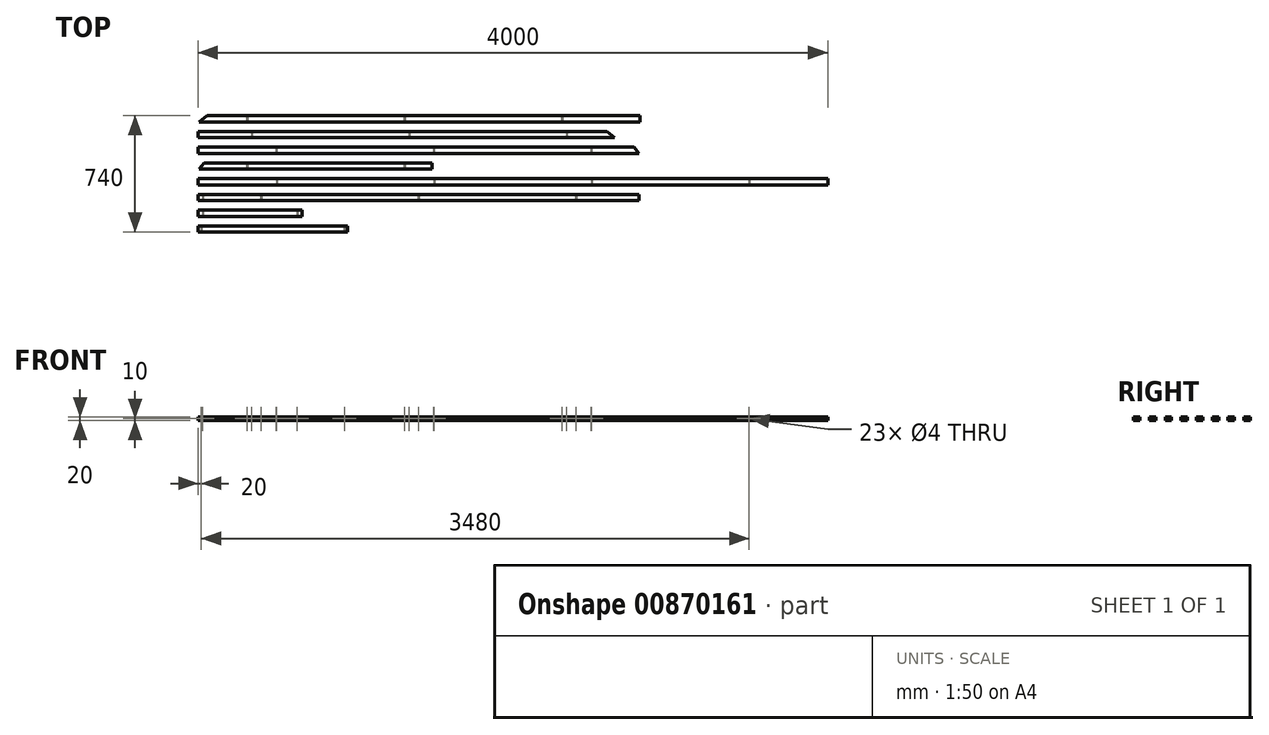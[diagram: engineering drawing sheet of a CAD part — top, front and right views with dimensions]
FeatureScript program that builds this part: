
annotation { "Feature Type Name" : "Feature", "Feature Type Description" : "" }
export const myFeature = defineFeature(function(context is Context, id is Id, definition is map)
    precondition{}
    {
        {
            var Q0;
            Q0=qCreatedBy(makeId("Right.planeOp"),FACE);
            var sketch = newSketch(context, id + "F0", { "sketchPlane" : qUnion([Q0])});
            skLineSegment(sketch, "E0.bottom", {"start": v(0, 0) * mm, "end": v(-40, 0) * mm});
            skLineSegment(sketch, "E0.top", {"start": v(0, 20) * mm, "end": v(-40, 20) * mm});
            skLineSegment(sketch, "E0.left", {"start": v(0, 0) * mm, "end": v(0, 20) * mm});
            skLineSegment(sketch, "E0.right", {"start": v(-40, 0) * mm, "end": v(-40, 20) * mm});
            skLineSegment(sketch, "E1.1.0.0", {"start": v(-100, 0) * mm, "end": v(-100, 20) * mm});
            skLineSegment(sketch, "E1.1.0.1", {"start": v(-100, 20) * mm, "end": v(-140, 20) * mm});
            skLineSegment(sketch, "E1.1.0.2", {"start": v(-140, 0) * mm, "end": v(-140, 20) * mm});
            skLineSegment(sketch, "E1.1.0.3", {"start": v(-100, 0) * mm, "end": v(-140, 0) * mm});
            skLineSegment(sketch, "E1.2.0.0", {"start": v(-200, 0) * mm, "end": v(-200, 20) * mm});
            skLineSegment(sketch, "E1.2.0.1", {"start": v(-200, 20) * mm, "end": v(-240, 20) * mm});
            skLineSegment(sketch, "E1.2.0.2", {"start": v(-240, 0) * mm, "end": v(-240, 20) * mm});
            skLineSegment(sketch, "E1.2.0.3", {"start": v(-200, 0) * mm, "end": v(-240, 0) * mm});
            skLineSegment(sketch, "E1.3.0.0", {"start": v(-300, 0) * mm, "end": v(-300, 20) * mm});
            skLineSegment(sketch, "E1.3.0.1", {"start": v(-300, 20) * mm, "end": v(-340, 20) * mm});
            skLineSegment(sketch, "E1.3.0.2", {"start": v(-340, 0) * mm, "end": v(-340, 20) * mm});
            skLineSegment(sketch, "E1.3.0.3", {"start": v(-300, 0) * mm, "end": v(-340, 0) * mm});
            skLineSegment(sketch, "E1.4.0.0", {"start": v(-400, 0) * mm, "end": v(-400, 20) * mm});
            skLineSegment(sketch, "E1.4.0.1", {"start": v(-400, 20) * mm, "end": v(-440, 20) * mm});
            skLineSegment(sketch, "E1.4.0.2", {"start": v(-440, 0) * mm, "end": v(-440, 20) * mm});
            skLineSegment(sketch, "E1.4.0.3", {"start": v(-400, 0) * mm, "end": v(-440, 0) * mm});
            skLineSegment(sketch, "E1.5.0.0", {"start": v(-500, 0) * mm, "end": v(-500, 20) * mm});
            skLineSegment(sketch, "E1.5.0.1", {"start": v(-500, 20) * mm, "end": v(-540, 20) * mm});
            skLineSegment(sketch, "E1.5.0.2", {"start": v(-540, 0) * mm, "end": v(-540, 20) * mm});
            skLineSegment(sketch, "E1.5.0.3", {"start": v(-500, 0) * mm, "end": v(-540, 0) * mm});
            skLineSegment(sketch, "E1.6.0.0", {"start": v(-600, 0) * mm, "end": v(-600, 20) * mm});
            skLineSegment(sketch, "E1.6.0.1", {"start": v(-600, 20) * mm, "end": v(-640, 20) * mm});
            skLineSegment(sketch, "E1.6.0.2", {"start": v(-640, 0) * mm, "end": v(-640, 20) * mm});
            skLineSegment(sketch, "E1.6.0.3", {"start": v(-600, 0) * mm, "end": v(-640, 0) * mm});
            skLineSegment(sketch, "E1.7.0.0", {"start": v(-700, 0) * mm, "end": v(-700, 20) * mm});
            skLineSegment(sketch, "E1.7.0.1", {"start": v(-700, 20) * mm, "end": v(-740, 20) * mm});
            skLineSegment(sketch, "E1.7.0.2", {"start": v(-740, 0) * mm, "end": v(-740, 20) * mm});
            skLineSegment(sketch, "E1.7.0.3", {"start": v(-700, 0) * mm, "end": v(-740, 0) * mm});
            skLineSegment(sketch, "E1.8.0.0", {"start": v(-800, 0) * mm, "end": v(-800, 20) * mm});
            skLineSegment(sketch, "E1.8.0.1", {"start": v(-800, 20) * mm, "end": v(-840, 20) * mm});
            skLineSegment(sketch, "E1.8.0.2", {"start": v(-840, 0) * mm, "end": v(-840, 20) * mm});
            skLineSegment(sketch, "E1.8.0.3", {"start": v(-800, 0) * mm, "end": v(-840, 0) * mm});
            skLineSegment(sketch, "E1.9.0.0", {"start": v(-900, 0) * mm, "end": v(-900, 20) * mm});
            skLineSegment(sketch, "E1.9.0.1", {"start": v(-900, 20) * mm, "end": v(-940, 20) * mm});
            skLineSegment(sketch, "E1.9.0.2", {"start": v(-940, 0) * mm, "end": v(-940, 20) * mm});
            skLineSegment(sketch, "E1.9.0.3", {"start": v(-900, 0) * mm, "end": v(-940, 0) * mm});
            skLineSegment(sketch, "E1.direction1", {"start": v(0, 0) * mm, "end": v(-100, 0) * mm, "construction": true});
            skSolve(sketch);
        }
        {
            var Q0;
            Q0=makeQuery(id+"F0.imprint","IMPRINT",FACE,{"disambiguationData":[TD([[makeQuery(id+"F0.imprint","IMPRINT",EDGE,{"derivedFrom":sQuery(id+"F0.wireOp",EDGE,"E0.bottom")}),-1.0]])]});
            extrude(context, id + "F1", {"entities" : qUnion([Q0]), "depth" : 2807 * mm, "offsetDistance" : 25 * mm});
        }
        {
            var Q0;
            Q0=makeQuery(id+"F1.opExtrude","SWEPT_FACE",FACE,{"disambiguationData":[OSD([sQuery(id+"F0.wireOp",EDGE,"E0.top")])]});
            var sketch = newSketch(context, id + "F2", { "sketchPlane" : qUnion([Q0])});
            skLineSegment(sketch, "E2", {"start": v(0, 0) * mm, "end": v(0, -40) * mm});
            skLineSegment(sketch, "E3", {"start": v(0, -40) * mm, "end": v(49.4, 0) * mm, "construction": true});
            skLineSegment(sketch, "E4", {"start": v(49.4, 0) * mm, "end": v(0, 0) * mm});
            skLineSegment(sketch, "E5", {"start": v(0, -40) * mm, "end": v(10.27, 8.32) * mm, "construction": true});
            skLineSegment(sketch, "E6", {"start": v(0, -40) * mm, "end": v(49.4, -40) * mm, "construction": true});
            skLineSegment(sketch, "E7", {"start": v(49.4, -40) * mm, "end": v(49.4, 0) * mm, "construction": true});
            skLineSegment(sketch, "E8", {"start": v(49.4, 0) * mm, "end": v(10.27, 8.32) * mm, "construction": true});
            skLineSegment(sketch, "E9", {"start": v(6.36, -40) * mm, "end": v(55.75, 0) * mm});
            skLineSegment(sketch, "E10", {"start": v(55.75, 0) * mm, "end": v(49.4, 0) * mm});
            skLineSegment(sketch, "E11", {"start": v(6.36, -40) * mm, "end": v(0, -40) * mm});
            skSolve(sketch);
        }
        {
            var Q0;
            Q0 = qSketchRegion(id + "F2", true);
            extrude(context, id + "F3", {"entities" : qUnion([Q0]), "operationType" : NewBodyOperationType.REMOVE, "endBound" : BoundingType.THROUGH_ALL, "oppositeDirection" : true, "depth" : 25 * mm, "offsetDistance" : 25 * mm});
        }
        {
            var Q0;
            Q0=makeQuery(id+"F1.opExtrude","SWEPT_FACE",FACE,{"disambiguationData":[OSD([sQuery(id+"F0.wireOp",EDGE,"E0.right")])]});
            var sketch = newSketch(context, id + "F4", { "sketchPlane" : qUnion([Q0])});
            skLineSegment(sketch, "E12.bottom", {"start": v(2281, 850) * mm, "end": v(2341, 850) * mm, "construction": true});
            skLineSegment(sketch, "E12.top", {"start": v(2281, -150) * mm, "end": v(2341, -150) * mm, "construction": true});
            skLineSegment(sketch, "E12.left", {"start": v(2281, 850) * mm, "end": v(2281, -150) * mm, "construction": true});
            skLineSegment(sketch, "E12.right", {"start": v(2341, 850) * mm, "end": v(2341, -150) * mm, "construction": true});
            skLineSegment(sketch, "E13", {"start": v(2311, -150) * mm, "end": v(2311, 0) * mm, "construction": true});
            skLineSegment(sketch, "E14", {"start": v(2311, 0) * mm, "end": v(2311, 10) * mm, "construction": true});
            skLineSegment(sketch, "E15", {"start": v(2311, 10) * mm, "end": v(2311, 20) * mm, "construction": true});
            skLineSegment(sketch, "E16.1.0.0", {"start": v(1311, 0) * mm, "end": v(1311, 10) * mm, "construction": true});
            skLineSegment(sketch, "E16.2.0.0", {"start": v(311, 0) * mm, "end": v(311, 10) * mm, "construction": true});
            skLineSegment(sketch, "E16.direction1", {"start": v(2311, 0) * mm, "end": v(1311, 0) * mm, "construction": true});
            skSolve(sketch);
        }
        {
            var Q0;
            Q0=sQuery(id+"F4.wireOp",VERTEX,"E14.end");
            var Q1;
            Q1=sQuery(id+"F4.wireOp",VERTEX,"E16.1.0.0.end");
            var Q2;
            Q2=sQuery(id+"F4.wireOp",VERTEX,"E16.2.0.0.end");
            var Q3;
            Q3=makeQuery(id+"F1.opExtrude","SWEPT_BODY",BODY,{"disambiguationData":[OSD([sQuery(id+"F0.wireOp",EDGE,"E0.bottom"),sQuery(id+"F0.wireOp",EDGE,"E0.top"),sQuery(id+"F0.wireOp",EDGE,"E0.left"),sQuery(id+"F0.wireOp",EDGE,"E0.right")])]});
            hole(context, id + "F5", {"style" : HoleStyle.C_SINK, "endStyle" : HoleEndStyle.THROUGH, "holeDiameter" : 4 * mm, "cSinkDiameter" : 8 * mm, "cSinkAngle" : 90 * degree, "majorDiameter" : 5 * mm, "isTappedThrough" : true, "tappedDepth" : 12 * mm, "tapClearance" : 3, "locations" : qUnion([Q0, Q1, Q2]), "scope" : qUnion([Q3])});
        }
        {
            var Q0;
            Q0=makeQuery(id+"F0.imprint","IMPRINT",FACE,{"disambiguationData":[TD([[makeQuery(id+"F0.imprint","IMPRINT",EDGE,{"derivedFrom":sQuery(id+"F0.wireOp",EDGE,"E1.1.0.0")}),1.0]])]});
            extrude(context, id + "F6", {"entities" : qUnion([Q0]), "depth" : 2652 * mm, "offsetDistance" : 25 * mm});
        }
        {
            var Q0;
            Q0=makeQuery(id+"F6.opExtrude","SWEPT_FACE",FACE,{"disambiguationData":[OSD([sQuery(id+"F0.wireOp",EDGE,"E1.1.0.1")])]});
            var sketch = newSketch(context, id + "F7", { "sketchPlane" : qUnion([Q0])});
            skLineSegment(sketch, "E17", {"start": v(2652, -140) * mm, "end": v(2645.64, -140) * mm});
            skLineSegment(sketch, "E18", {"start": v(2645.64, -140) * mm, "end": v(2596.25, -100) * mm});
            skLineSegment(sketch, "E19", {"start": v(2596.25, -100) * mm, "end": v(2602.6, -100) * mm});
            skLineSegment(sketch, "E20", {"start": v(2602.6, -100) * mm, "end": v(2652, -100) * mm});
            skLineSegment(sketch, "E21", {"start": v(2652, -100) * mm, "end": v(2652, -140) * mm});
            skLineSegment(sketch, "E22", {"start": v(2602.6, -100) * mm, "end": v(2652, -140) * mm, "construction": true});
            skLineSegment(sketch, "E23", {"start": v(2652, -140) * mm, "end": v(2602.6, -140) * mm, "construction": true});
            skLineSegment(sketch, "E24", {"start": v(2652, -140) * mm, "end": v(2641.73, -91.68) * mm, "construction": true});
            skLineSegment(sketch, "E25", {"start": v(2641.73, -91.68) * mm, "end": v(2602.6, -100) * mm, "construction": true});
            skLineSegment(sketch, "E26", {"start": v(2602.6, -100) * mm, "end": v(2602.6, -140) * mm, "construction": true});
            skSolve(sketch);
        }
        {
            var Q0;
            Q0 = qSketchRegion(id + "F7", true);
            extrude(context, id + "F8", {"entities" : qUnion([Q0]), "operationType" : NewBodyOperationType.REMOVE, "endBound" : BoundingType.THROUGH_ALL, "oppositeDirection" : true, "depth" : 25 * mm, "offsetDistance" : 25 * mm});
        }
        {
            var Q0;
            Q0=makeQuery(id+"F6.opExtrude","SWEPT_FACE",FACE,{"disambiguationData":[OSD([sQuery(id+"F0.wireOp",EDGE,"E1.1.0.2")])]});
            var sketch = newSketch(context, id + "F9", { "sketchPlane" : qUnion([Q0])});
            skLineSegment(sketch, "E27.bottom", {"start": v(2310.64, 850) * mm, "end": v(2370.64, 850) * mm, "construction": true});
            skLineSegment(sketch, "E27.top", {"start": v(2310.64, -150) * mm, "end": v(2370.64, -150) * mm, "construction": true});
            skLineSegment(sketch, "E27.left", {"start": v(2310.64, 850) * mm, "end": v(2310.64, -150) * mm, "construction": true});
            skLineSegment(sketch, "E27.right", {"start": v(2370.64, 850) * mm, "end": v(2370.64, -150) * mm, "construction": true});
            skLineSegment(sketch, "E28", {"start": v(2340.64, -150) * mm, "end": v(2340.64, 0) * mm, "construction": true});
            skLineSegment(sketch, "E29", {"start": v(2340.64, 0) * mm, "end": v(2340.64, 10) * mm, "construction": true});
            skLineSegment(sketch, "E30", {"start": v(2340.64, 10) * mm, "end": v(2340.64, 20) * mm, "construction": true});
            skLineSegment(sketch, "E31.1.0.0", {"start": v(1340.64, 0) * mm, "end": v(1340.64, 10) * mm, "construction": true});
            skLineSegment(sketch, "E31.2.0.0", {"start": v(340.64, 0) * mm, "end": v(340.64, 10) * mm, "construction": true});
            skLineSegment(sketch, "E31.direction1", {"start": v(2340.64, 0) * mm, "end": v(1340.64, 0) * mm, "construction": true});
            skSolve(sketch);
        }
        {
            var Q0;
            Q0=sQuery(id+"F9.wireOp",VERTEX,"E29.end");
            var Q1;
            Q1=sQuery(id+"F9.wireOp",VERTEX,"E31.1.0.0.end");
            var Q2;
            Q2=sQuery(id+"F9.wireOp",VERTEX,"E31.2.0.0.end");
            var Q3;
            Q3=makeQuery(id+"F6.opExtrude","SWEPT_BODY",BODY,{"disambiguationData":[OSD([sQuery(id+"F0.wireOp",EDGE,"E1.1.0.0"),sQuery(id+"F0.wireOp",EDGE,"E1.1.0.1"),sQuery(id+"F0.wireOp",EDGE,"E1.1.0.2"),sQuery(id+"F0.wireOp",EDGE,"E1.1.0.3")])]});
            hole(context, id + "F10", {"style" : HoleStyle.C_SINK, "endStyle" : HoleEndStyle.THROUGH, "holeDiameter" : 4 * mm, "cSinkDiameter" : 8 * mm, "cSinkAngle" : 90 * degree, "majorDiameter" : 5 * mm, "isTappedThrough" : true, "tappedDepth" : 12 * mm, "tapClearance" : 3, "locations" : qUnion([Q0, Q1, Q2]), "scope" : qUnion([Q3])});
        }
        {
            var Q0;
            Q0=makeQuery(id+"F0.imprint","IMPRINT",FACE,{"disambiguationData":[TD([[makeQuery(id+"F0.imprint","IMPRINT",EDGE,{"derivedFrom":sQuery(id+"F0.wireOp",EDGE,"E1.2.0.0")}),1.0]])]});
            extrude(context, id + "F11", {"entities" : qUnion([Q0]), "depth" : 2807 * mm, "offsetDistance" : 25 * mm});
        }
        {
            var Q0;
            Q0=makeQuery(id+"F11.opExtrude","SWEPT_FACE",FACE,{"disambiguationData":[OSD([sQuery(id+"F0.wireOp",EDGE,"E1.2.0.1")])]});
            var sketch = newSketch(context, id + "F12", { "sketchPlane" : qUnion([Q0])});
            skLineSegment(sketch, "E32", {"start": v(2807, -240) * mm, "end": v(2807, -200) * mm});
            skLineSegment(sketch, "E33", {"start": v(2807, -200) * mm, "end": v(2774.6, -200) * mm});
            skLineSegment(sketch, "E34", {"start": v(2774.6, -200) * mm, "end": v(2769.46, -200) * mm});
            skLineSegment(sketch, "E35", {"start": v(2769.46, -200) * mm, "end": v(2801.85, -240) * mm});
            skLineSegment(sketch, "E36", {"start": v(2801.85, -240) * mm, "end": v(2807, -240) * mm});
            skLineSegment(sketch, "E37", {"start": v(2807, -240) * mm, "end": v(2774.6, -200) * mm, "construction": true});
            skLineSegment(sketch, "E38", {"start": v(2774.6, -200) * mm, "end": v(2813.73, -208.32) * mm, "construction": true});
            skLineSegment(sketch, "E39", {"start": v(2813.73, -208.32) * mm, "end": v(2807, -240) * mm, "construction": true});
            skLineSegment(sketch, "E40", {"start": v(2807, -240) * mm, "end": v(2774.6, -240) * mm, "construction": true});
            skLineSegment(sketch, "E41", {"start": v(2774.6, -240) * mm, "end": v(2774.6, -200) * mm, "construction": true});
            skSolve(sketch);
        }
        {
            var Q0;
            Q0=makeQuery(id+"F12.imprint","IMPRINT",FACE,{"disambiguationData":[TD([[makeQuery(id+"F12.imprint","IMPRINT",EDGE,{"derivedFrom":sQuery(id+"F12.wireOp",EDGE,"E32")}),-1.0]])]});
            extrude(context, id + "F13", {"entities" : qUnion([Q0]), "operationType" : NewBodyOperationType.REMOVE, "oppositeDirection" : true, "depth" : 25 * mm, "offsetDistance" : 25 * mm});
        }
        {
            var Q0;
            Q0=makeQuery(id+"F11.opExtrude","SWEPT_FACE",FACE,{"disambiguationData":[OSD([sQuery(id+"F0.wireOp",EDGE,"E1.2.0.2")])]});
            var sketch = newSketch(context, id + "F14", { "sketchPlane" : qUnion([Q0])});
            skLineSegment(sketch, "E42.bottom", {"start": v(466, 850) * mm, "end": v(526, 850) * mm, "construction": true});
            skLineSegment(sketch, "E42.top", {"start": v(466, -150) * mm, "end": v(526, -150) * mm, "construction": true});
            skLineSegment(sketch, "E42.left", {"start": v(466, 850) * mm, "end": v(466, -150) * mm, "construction": true});
            skLineSegment(sketch, "E42.right", {"start": v(526, 850) * mm, "end": v(526, -150) * mm, "construction": true});
            skLineSegment(sketch, "E43", {"start": v(496, -150) * mm, "end": v(496, 0) * mm, "construction": true});
            skLineSegment(sketch, "E44", {"start": v(496, 0) * mm, "end": v(496, 10) * mm, "construction": true});
            skLineSegment(sketch, "E45", {"start": v(496, 10) * mm, "end": v(496, 20) * mm, "construction": true});
            skLineSegment(sketch, "E46.1.0.0", {"start": v(1496, 0) * mm, "end": v(1496, 10) * mm, "construction": true});
            skLineSegment(sketch, "E46.2.0.0", {"start": v(2496, 0) * mm, "end": v(2496, 10) * mm, "construction": true});
            skLineSegment(sketch, "E46.direction1", {"start": v(496, 0) * mm, "end": v(1496, 0) * mm, "construction": true});
            skSolve(sketch);
        }
        {
            var Q0;
            Q0=sQuery(id+"F14.wireOp",VERTEX,"E44.end");
            var Q1;
            Q1=sQuery(id+"F14.wireOp",VERTEX,"E46.1.0.0.end");
            var Q2;
            Q2=sQuery(id+"F14.wireOp",VERTEX,"E46.2.0.0.end");
            var Q3;
            Q3=makeQuery(id+"F11.opExtrude","SWEPT_BODY",BODY,{"disambiguationData":[OSD([sQuery(id+"F0.wireOp",EDGE,"E1.2.0.0"),sQuery(id+"F0.wireOp",EDGE,"E1.2.0.1"),sQuery(id+"F0.wireOp",EDGE,"E1.2.0.2"),sQuery(id+"F0.wireOp",EDGE,"E1.2.0.3")])]});
            hole(context, id + "F15", {"style" : HoleStyle.C_SINK, "endStyle" : HoleEndStyle.THROUGH, "holeDiameter" : 4 * mm, "cSinkDiameter" : 8 * mm, "cSinkAngle" : 90 * degree, "majorDiameter" : 5 * mm, "isTappedThrough" : true, "tappedDepth" : 12 * mm, "tapClearance" : 3, "locations" : qUnion([Q0, Q1, Q2]), "scope" : qUnion([Q3])});
        }
        {
            var Q0;
            Q0=makeQuery(id+"F0.imprint","IMPRINT",FACE,{"disambiguationData":[TD([[makeQuery(id+"F0.imprint","IMPRINT",EDGE,{"derivedFrom":sQuery(id+"F0.wireOp",EDGE,"E1.3.0.0")}),1.0]])]});
            extrude(context, id + "F16", {"entities" : qUnion([Q0]), "depth" : 1486 * mm, "offsetDistance" : 25 * mm});
        }
        {
            var Q0;
            Q0=makeQuery(id+"F16.opExtrude","SWEPT_FACE",FACE,{"disambiguationData":[OSD([sQuery(id+"F0.wireOp",EDGE,"E1.3.0.1")])]});
            var sketch = newSketch(context, id + "F17", { "sketchPlane" : qUnion([Q0])});
            skLineSegment(sketch, "E47", {"start": v(0, -340) * mm, "end": v(0, -300) * mm});
            skLineSegment(sketch, "E48", {"start": v(0, -300) * mm, "end": v(32.4, -300) * mm});
            skLineSegment(sketch, "E49", {"start": v(32.4, -300) * mm, "end": v(37.54, -300) * mm});
            skLineSegment(sketch, "E50", {"start": v(37.54, -300) * mm, "end": v(5.15, -340) * mm});
            skLineSegment(sketch, "E51", {"start": v(5.15, -340) * mm, "end": v(0, -340) * mm});
            skLineSegment(sketch, "E52", {"start": v(0, -340) * mm, "end": v(32.4, -300) * mm, "construction": true});
            skLineSegment(sketch, "E53", {"start": v(32.4, -300) * mm, "end": v(-6.73, -308.32) * mm, "construction": true});
            skLineSegment(sketch, "E54", {"start": v(-6.73, -308.32) * mm, "end": v(0, -340) * mm, "construction": true});
            skLineSegment(sketch, "E55", {"start": v(0, -340) * mm, "end": v(32.4, -340) * mm, "construction": true});
            skLineSegment(sketch, "E56", {"start": v(32.4, -340) * mm, "end": v(32.4, -300) * mm, "construction": true});
            skSolve(sketch);
        }
        {
            var Q0;
            Q0 = qSketchRegion(id + "F17", true);
            extrude(context, id + "F18", {"entities" : qUnion([Q0]), "operationType" : NewBodyOperationType.REMOVE, "endBound" : BoundingType.THROUGH_ALL, "oppositeDirection" : true, "depth" : 25 * mm, "offsetDistance" : 25 * mm});
        }
        {
            var Q0;
            Q0=makeQuery(id+"F16.opExtrude","SWEPT_FACE",FACE,{"disambiguationData":[OSD([sQuery(id+"F0.wireOp",EDGE,"E1.3.0.2")])]});
            var sketch = newSketch(context, id + "F19", { "sketchPlane" : qUnion([Q0])});
            skLineSegment(sketch, "E57.bottom", {"start": v(281.15, 850) * mm, "end": v(341.15, 850) * mm, "construction": true});
            skLineSegment(sketch, "E57.top", {"start": v(281.15, -150) * mm, "end": v(341.15, -150) * mm, "construction": true});
            skLineSegment(sketch, "E57.left", {"start": v(281.15, 850) * mm, "end": v(281.15, -150) * mm, "construction": true});
            skLineSegment(sketch, "E57.right", {"start": v(341.15, 850) * mm, "end": v(341.15, -150) * mm, "construction": true});
            skLineSegment(sketch, "E58", {"start": v(311.15, -150) * mm, "end": v(311.15, 0) * mm, "construction": true});
            skLineSegment(sketch, "E59", {"start": v(311.15, 0) * mm, "end": v(311.15, 10) * mm, "construction": true});
            skLineSegment(sketch, "E60", {"start": v(311.15, 10) * mm, "end": v(311.15, 20) * mm, "construction": true});
            skLineSegment(sketch, "E61.1.0.0", {"start": v(1311.15, 0) * mm, "end": v(1311.15, 10) * mm, "construction": true});
            skLineSegment(sketch, "E61.direction1", {"start": v(311.15, 0) * mm, "end": v(1311.15, 0) * mm, "construction": true});
            skSolve(sketch);
        }
        {
            var Q0;
            Q0=sQuery(id+"F19.wireOp",VERTEX,"E59.end");
            var Q1;
            Q1=sQuery(id+"F19.wireOp",VERTEX,"E61.1.0.0.end");
            var Q2;
            Q2=makeQuery(id+"F16.opExtrude","SWEPT_BODY",BODY,{"disambiguationData":[OSD([sQuery(id+"F0.wireOp",EDGE,"E1.3.0.0"),sQuery(id+"F0.wireOp",EDGE,"E1.3.0.1"),sQuery(id+"F0.wireOp",EDGE,"E1.3.0.2"),sQuery(id+"F0.wireOp",EDGE,"E1.3.0.3")])]});
            hole(context, id + "F20", {"style" : HoleStyle.C_SINK, "endStyle" : HoleEndStyle.THROUGH, "holeDiameter" : 4 * mm, "cSinkDiameter" : 8 * mm, "cSinkAngle" : 90 * degree, "majorDiameter" : 5 * mm, "isTappedThrough" : true, "tappedDepth" : 12 * mm, "tapClearance" : 3, "locations" : qUnion([Q0, Q1]), "scope" : qUnion([Q2])});
        }
        {
            var Q0;
            Q0=makeQuery(id+"F0.imprint","IMPRINT",FACE,{"disambiguationData":[TD([[makeQuery(id+"F0.imprint","IMPRINT",EDGE,{"derivedFrom":sQuery(id+"F0.wireOp",EDGE,"E1.4.0.0")}),1.0]])]});
            extrude(context, id + "F21", {"entities" : qUnion([Q0]), "depth" : 4000 * mm, "offsetDistance" : 25 * mm});
        }
        {
            var Q0;
            Q0=makeQuery(id+"F21.opExtrude","SWEPT_FACE",FACE,{"disambiguationData":[OSD([sQuery(id+"F0.wireOp",EDGE,"E1.4.0.2")])]});
            var sketch = newSketch(context, id + "F22", { "sketchPlane" : qUnion([Q0])});
            skLineSegment(sketch, "E62.bottom", {"start": v(470, 850) * mm, "end": v(530, 850) * mm, "construction": true});
            skLineSegment(sketch, "E62.top", {"start": v(470, -150) * mm, "end": v(530, -150) * mm, "construction": true});
            skLineSegment(sketch, "E62.left", {"start": v(470, 850) * mm, "end": v(470, -150) * mm, "construction": true});
            skLineSegment(sketch, "E62.right", {"start": v(530, 850) * mm, "end": v(530, -150) * mm, "construction": true});
            skLineSegment(sketch, "E63", {"start": v(500, -150) * mm, "end": v(500, 0) * mm, "construction": true});
            skLineSegment(sketch, "E64", {"start": v(500, 0) * mm, "end": v(500, 10) * mm, "construction": true});
            skLineSegment(sketch, "E65", {"start": v(500, 10) * mm, "end": v(500, 20) * mm, "construction": true});
            skLineSegment(sketch, "E66.1.0.0", {"start": v(1500, 0) * mm, "end": v(1500, 10) * mm, "construction": true});
            skLineSegment(sketch, "E66.2.0.0", {"start": v(2500, 0) * mm, "end": v(2500, 10) * mm, "construction": true});
            skLineSegment(sketch, "E66.3.0.0", {"start": v(3500, 0) * mm, "end": v(3500, 10) * mm, "construction": true});
            skLineSegment(sketch, "E66.direction1", {"start": v(500, 0) * mm, "end": v(1500, 0) * mm, "construction": true});
            skSolve(sketch);
        }
        {
            var Q0;
            Q0=sQuery(id+"F22.wireOp",VERTEX,"E64.end");
            var Q1;
            Q1=sQuery(id+"F22.wireOp",VERTEX,"E66.1.0.0.end");
            var Q2;
            Q2=sQuery(id+"F22.wireOp",VERTEX,"E66.2.0.0.end");
            var Q3;
            Q3=sQuery(id+"F22.wireOp",VERTEX,"E66.3.0.0.end");
            var Q4;
            Q4=makeQuery(id+"F21.opExtrude","SWEPT_BODY",BODY,{"disambiguationData":[OSD([sQuery(id+"F0.wireOp",EDGE,"E1.4.0.0"),sQuery(id+"F0.wireOp",EDGE,"E1.4.0.1"),sQuery(id+"F0.wireOp",EDGE,"E1.4.0.2"),sQuery(id+"F0.wireOp",EDGE,"E1.4.0.3")])]});
            hole(context, id + "F23", {"style" : HoleStyle.C_SINK, "endStyle" : HoleEndStyle.THROUGH, "holeDiameter" : 4 * mm, "cSinkDiameter" : 8 * mm, "cSinkAngle" : 90 * degree, "majorDiameter" : 5 * mm, "isTappedThrough" : true, "tappedDepth" : 12 * mm, "tapClearance" : 3, "locations" : qUnion([Q0, Q1, Q2, Q3]), "scope" : qUnion([Q4])});
        }
        {
            var Q0;
            Q0=makeQuery(id+"F0.imprint","IMPRINT",FACE,{"disambiguationData":[TD([[makeQuery(id+"F0.imprint","IMPRINT",EDGE,{"derivedFrom":sQuery(id+"F0.wireOp",EDGE,"E1.5.0.0")}),1.0]])]});
            extrude(context, id + "F24", {"entities" : qUnion([Q0]), "depth" : 2800 * mm, "offsetDistance" : 25 * mm});
        }
        {
            var Q0;
            Q0=makeQuery(id+"F24.opExtrude","SWEPT_FACE",FACE,{"disambiguationData":[OSD([sQuery(id+"F0.wireOp",EDGE,"E1.5.0.2")])]});
            var sketch = newSketch(context, id + "F25", { "sketchPlane" : qUnion([Q0])});
            skLineSegment(sketch, "E67.bottom", {"start": v(370, 850) * mm, "end": v(430, 850) * mm, "construction": true});
            skLineSegment(sketch, "E67.top", {"start": v(370, -150) * mm, "end": v(430, -150) * mm, "construction": true});
            skLineSegment(sketch, "E67.left", {"start": v(370, 850) * mm, "end": v(370, -150) * mm, "construction": true});
            skLineSegment(sketch, "E67.right", {"start": v(430, 850) * mm, "end": v(430, -150) * mm, "construction": true});
            skLineSegment(sketch, "E68", {"start": v(400, -150) * mm, "end": v(400, 0) * mm, "construction": true});
            skLineSegment(sketch, "E69", {"start": v(400, 0) * mm, "end": v(400, 10) * mm, "construction": true});
            skLineSegment(sketch, "E70", {"start": v(400, 10) * mm, "end": v(400, 20) * mm, "construction": true});
            skLineSegment(sketch, "E71", {"start": v(30, 0) * mm, "end": v(30, 10) * mm, "construction": true});
            skLineSegment(sketch, "E72.1.0.0", {"start": v(1400, 0) * mm, "end": v(1400, 10) * mm, "construction": true});
            skLineSegment(sketch, "E72.2.0.0", {"start": v(2400, 0) * mm, "end": v(2400, 10) * mm, "construction": true});
            skLineSegment(sketch, "E72.direction1", {"start": v(400, 0) * mm, "end": v(1400, 0) * mm, "construction": true});
            skSolve(sketch);
        }
        {
            var Q0;
            Q0=sQuery(id+"F25.wireOp",VERTEX,"E71.end");
            var Q1;
            Q1=sQuery(id+"F25.wireOp",VERTEX,"E69.end");
            var Q2;
            Q2=sQuery(id+"F25.wireOp",VERTEX,"E72.1.0.0.end");
            var Q3;
            Q3=sQuery(id+"F25.wireOp",VERTEX,"E72.2.0.0.end");
            var Q4;
            Q4=makeQuery(id+"F24.opExtrude","SWEPT_BODY",BODY,{"disambiguationData":[OSD([sQuery(id+"F0.wireOp",EDGE,"E1.5.0.0"),sQuery(id+"F0.wireOp",EDGE,"E1.5.0.1"),sQuery(id+"F0.wireOp",EDGE,"E1.5.0.2"),sQuery(id+"F0.wireOp",EDGE,"E1.5.0.3")])]});
            hole(context, id + "F26", {"style" : HoleStyle.C_SINK, "endStyle" : HoleEndStyle.THROUGH, "holeDiameter" : 4 * mm, "cSinkDiameter" : 8 * mm, "cSinkAngle" : 90 * degree, "majorDiameter" : 5 * mm, "isTappedThrough" : true, "tappedDepth" : 12 * mm, "tapClearance" : 3, "locations" : qUnion([Q0, Q1, Q2, Q3]), "scope" : qUnion([Q4])});
        }
        {
            var Q0;
            Q0=makeQuery(id+"F0.imprint","IMPRINT",FACE,{"disambiguationData":[TD([[makeQuery(id+"F0.imprint","IMPRINT",EDGE,{"derivedFrom":sQuery(id+"F0.wireOp",EDGE,"E1.6.0.0")}),1.0]])]});
            extrude(context, id + "F27", {"entities" : qUnion([Q0]), "depth" : 660 * mm, "offsetDistance" : 25 * mm});
        }
        {
            var Q0;
            Q0=makeQuery(id+"F27.opExtrude","SWEPT_FACE",FACE,{"disambiguationData":[OSD([sQuery(id+"F0.wireOp",EDGE,"E1.6.0.2")])]});
            var sketch = newSketch(context, id + "F28", { "sketchPlane" : qUnion([Q0])});
            skLineSegment(sketch, "E73", {"start": v(30, 0) * mm, "end": v(30, 10) * mm, "construction": true});
            skLineSegment(sketch, "E74", {"start": v(30, 10) * mm, "end": v(30, 20) * mm, "construction": true});
            skLineSegment(sketch, "E75", {"start": v(0, 10) * mm, "end": v(30, 10) * mm, "construction": true});
            skLineSegment(sketch, "E76", {"start": v(630, 0) * mm, "end": v(630, 10) * mm, "construction": true});
            skLineSegment(sketch, "E77", {"start": v(630, 10) * mm, "end": v(660, 10) * mm, "construction": true});
            skLineSegment(sketch, "E78", {"start": v(630, 10) * mm, "end": v(630, 20) * mm, "construction": true});
            skSolve(sketch);
        }
        {
            var Q0;
            Q0=sQuery(id+"F28.wireOp",VERTEX,"E76.end");
            var Q1;
            Q1=sQuery(id+"F28.wireOp",VERTEX,"E73.end");
            var Q2;
            Q2=makeQuery(id+"F27.opExtrude","SWEPT_BODY",BODY,{"disambiguationData":[OSD([sQuery(id+"F0.wireOp",EDGE,"E1.6.0.0"),sQuery(id+"F0.wireOp",EDGE,"E1.6.0.1"),sQuery(id+"F0.wireOp",EDGE,"E1.6.0.2"),sQuery(id+"F0.wireOp",EDGE,"E1.6.0.3")])]});
            hole(context, id + "F29", {"style" : HoleStyle.C_SINK, "endStyle" : HoleEndStyle.THROUGH, "holeDiameter" : 4 * mm, "cSinkDiameter" : 8 * mm, "cSinkAngle" : 90 * degree, "majorDiameter" : 5 * mm, "isTappedThrough" : true, "tappedDepth" : 12 * mm, "tapClearance" : 3, "locations" : qUnion([Q0, Q1]), "scope" : qUnion([Q2])});
        }
        {
            var Q0;
            Q0=makeQuery(id+"F0.imprint","IMPRINT",FACE,{"disambiguationData":[TD([[makeQuery(id+"F0.imprint","IMPRINT",EDGE,{"derivedFrom":sQuery(id+"F0.wireOp",EDGE,"E1.7.0.0")}),1.0]])]});
            extrude(context, id + "F30", {"entities" : qUnion([Q0]), "depth" : 950 * mm, "offsetDistance" : 25 * mm});
        }
        {
            var Q0;
            Q0=makeQuery(id+"F30.opExtrude","SWEPT_FACE",FACE,{"disambiguationData":[OSD([sQuery(id+"F0.wireOp",EDGE,"E1.7.0.2")])]});
            var sketch = newSketch(context, id + "F31", { "sketchPlane" : qUnion([Q0])});
            skLineSegment(sketch, "E79", {"start": v(0, 10) * mm, "end": v(20, 10) * mm, "construction": true});
            skLineSegment(sketch, "E80", {"start": v(950, 10) * mm, "end": v(930, 10) * mm, "construction": true});
            skSolve(sketch);
        }
        {
            var Q0;
            Q0=sQuery(id+"F31.wireOp",VERTEX,"E79.end");
            var Q1;
            Q1=sQuery(id+"F31.wireOp",VERTEX,"E80.end");
            var Q2;
            Q2=makeQuery(id+"F30.opExtrude","SWEPT_BODY",BODY,{"disambiguationData":[OSD([sQuery(id+"F0.wireOp",EDGE,"E1.7.0.0"),sQuery(id+"F0.wireOp",EDGE,"E1.7.0.1"),sQuery(id+"F0.wireOp",EDGE,"E1.7.0.2"),sQuery(id+"F0.wireOp",EDGE,"E1.7.0.3")])]});
            hole(context, id + "F32", {"style" : HoleStyle.C_SINK, "endStyle" : HoleEndStyle.THROUGH, "holeDiameter" : 4 * mm, "cSinkDiameter" : 8 * mm, "cSinkAngle" : 90 * degree, "majorDiameter" : 5 * mm, "isTappedThrough" : true, "tappedDepth" : 12 * mm, "tapClearance" : 3, "locations" : qUnion([Q0, Q1]), "scope" : qUnion([Q2])});
        }
    });
